# Revit family: FL -5700-10500
name_source: partatom
category: HLS-Bauteile
revit_build: Autodesk Revit 2017 (Build: 20190507_1515(x64)
units: mm (PartAtom-declared; Revit-internal decimal feet)

## family parameters
Arbeitsebenenbasiert = Ja
Beim Laden mit Abzugskörper schneiden = Nein
Bemaßung runder Anschluss = Durchmesser verwenden
Gemeinsam genutzt = Ja
Immer vertikal = Nein
Raumberechnungspunkt = Nein
Teiletyp = Normal

## types (2) — shared parameters
Anschluss = M12
Breite = 98 mm  [stored 0.321522 ft]
Fabrikat = MEFA
Firma = MEFA Befestigungs- und Montagesysteme GmbH
Gewicht = 6.10 kg
Gewicht pro Bauteil = 6.10 kg
Höhe = 102 mm
Länge = 330 mm
Material = Stahl
Materialname = S235
Mengeneinheit = St
Oberflaeche = galvanisch verzinkt
Vorgabe-Ansicht = 1219 mm
max. Federweg = 27 mm
min. Lastbereich = 0 N
vpe = 1 St

## per-type parameters (varying)
| type | Artikelnummer | EAN | Federrate | Kurztext1 | Kurztext2 | max. Lastbereich |
| Federlager FL -  5700 | 07919057 | 4250928419040 | 226,38 N/mm | Federlager FL Typ 2 - 5700 | F 0 - 5.999 N max. Federweg 26,5 mm | 5.999 N |
| Federlager FL - 10500 | 07919105 | 4250928419064 | 402,9 N/mm | Federlager FL Typ 2 - 10500 | F 0 - 10.677 N max. Federweg 26,5 mm | 10.677 N |

note: [stored X ft] marks values corroborated as IEEE doubles in the binary element streams (Revit-internal decimal feet)
